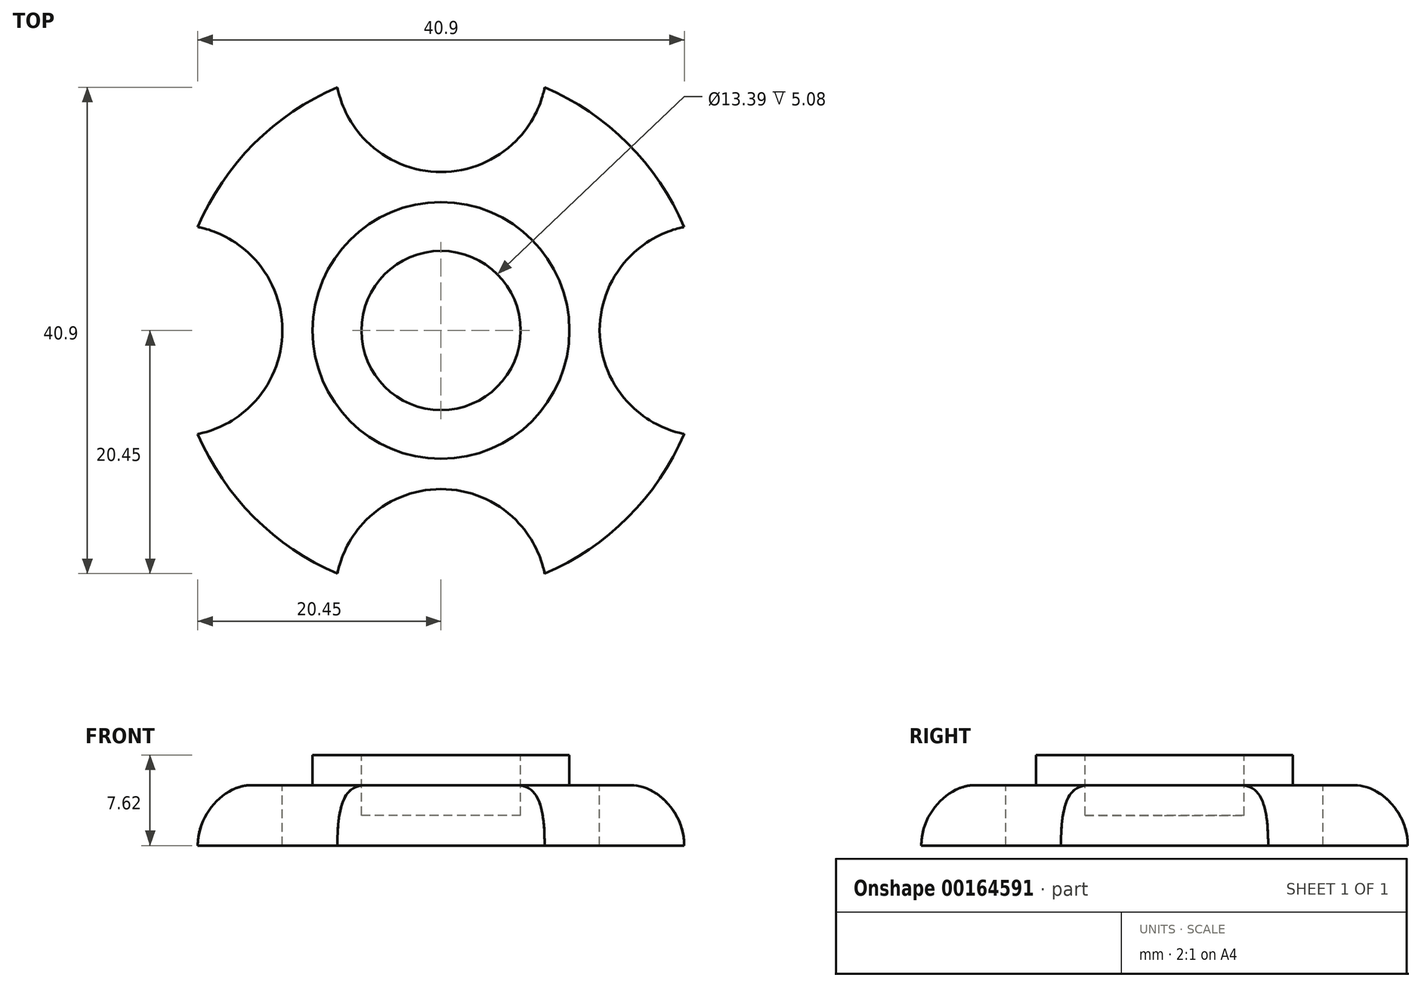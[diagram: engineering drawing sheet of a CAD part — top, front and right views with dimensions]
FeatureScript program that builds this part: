
annotation { "Feature Type Name" : "Feature", "Feature Type Description" : "" }
export const myFeature = defineFeature(function(context is Context, id is Id, definition is map)
    precondition{}
    {
        {
            var Q0;
            Q0=qCreatedBy(makeId("Top.planeOp"),FACE);
            var sketch = newSketch(context, id + "F0", { "sketchPlane" : qUnion([Q0])});
            skCircle(sketch, "E0", {"center": v(0, 0) * mm, "radius": 22.23 * mm});
            skSolve(sketch);
        }
        {
            var Q0;
            Q0 = qSketchRegion(id + "F0", true);
            extrude(context, id + "F1", {"entities" : qUnion([Q0]), "depth" : 5.08 * mm});
        }
        {
            var Q0;
            Q0=makeQuery(id+"F1.opExtrude","CAP_FACE",FACE,{"disambiguationData":[OSD([sQuery(id+"F0.wireOp",EDGE,"E0")])],"isStart":false});
            var sketch = newSketch(context, id + "F2", { "sketchPlane" : qUnion([Q0])});
            skCircle(sketch, "E1", {"center": v(0, 0) * mm, "radius": 10.8 * mm});
            skSolve(sketch);
        }
        {
            var Q0;
            Q0 = qSketchRegion(id + "F2", true);
            extrude(context, id + "F3", {"entities" : qUnion([Q0]), "operationType" : NewBodyOperationType.ADD, "depth" : 2.54 * mm});
        }
        {
            var Q0;
            Q0=makeQuery(id+"F3.opExtrude","CAP_FACE",FACE,{"disambiguationData":[OSD([sQuery(id+"F2.wireOp",EDGE,"E1")])],"isStart":false});
            var sketch = newSketch(context, id + "F4", { "sketchPlane" : qUnion([Q0])});
            skCircle(sketch, "E2", {"center": v(0, 0) * mm, "radius": 6.7 * mm});
            skSolve(sketch);
        }
        {
            var Q0;
            Q0 = qSketchRegion(id + "F4", true);
            extrude(context, id + "F5", {"entities" : qUnion([Q0]), "operationType" : NewBodyOperationType.REMOVE, "oppositeDirection" : true, "depth" : 5.08 * mm});
        }
        {
            var Q0;
            Q0=makeQuery(id+"F1.opExtrude","CAP_FACE",FACE,{"disambiguationData":[OSD([sQuery(id+"F0.wireOp",EDGE,"E0")])],"isStart":false});
            var sketch = newSketch(context, id + "F6", { "sketchPlane" : qUnion([Q0])});
            skCircle(sketch, "E3", {"center": v(0, 22.23) * mm, "radius": 8.9 * mm});
            skCircle(sketch, "E4", {"center": v(22.23, 0) * mm, "radius": 8.9 * mm});
            skCircle(sketch, "E5", {"center": v(0, -22.23) * mm, "radius": 8.9 * mm});
            skCircle(sketch, "E6", {"center": v(-22.23, 0) * mm, "radius": 8.9 * mm});
            skSolve(sketch);
        }
        {
            var Q0;
            Q0 = qSketchRegion(id + "F6", true);
            extrude(context, id + "F7", {"entities" : qUnion([Q0]), "operationType" : NewBodyOperationType.REMOVE, "oppositeDirection" : true, "depth" : 25.4 * mm});
        }
        {
            var Q0;
            {var subQ0=sQuery(id+"F0.wireOp",EDGE,"E0");Q0=makeQuery(id+"F7.boolean.opBoolean","SPLIT",EDGE,{"disambiguationData":[TD([makeQuery(id+"F1.opExtrude","SWEPT_FACE",FACE,{"disambiguationData":[OSD([subQ0])]}),makeQuery(id+"F1.opExtrude","CAP_FACE",FACE,{"disambiguationData":[OSD([subQ0])],"isStart":false}),makeQuery(id+"F7.opExtrude","SWEPT_FACE",FACE,{"disambiguationData":[OSD([sQuery(id+"F6.wireOp",EDGE,"E3")])]}),makeQuery(id+"F7.opExtrude","SWEPT_FACE",FACE,{"disambiguationData":[OSD([sQuery(id+"F6.wireOp",EDGE,"E6")])]})])],"derivedFrom":makeQuery(id+"F1.opExtrude","CAP_EDGE",EDGE,{"disambiguationData":[OSD([subQ0])],"isStart":false})});}
            var Q1;
            Q1=makeQuery(id+"F7.boolean.opBoolean","COPY",EDGE,{"derivedFrom":makeQuery(id+"F7.opExtrude","CAP_EDGE",EDGE,{"disambiguationData":[OSD([sQuery(id+"F6.wireOp",EDGE,"E3")])],"isStart":true})});
            var Q2;
            Q2=makeQuery(id+"F7.boolean.opBoolean","COPY",EDGE,{"derivedFrom":makeQuery(id+"F7.opExtrude","CAP_EDGE",EDGE,{"disambiguationData":[OSD([sQuery(id+"F6.wireOp",EDGE,"E4")])],"isStart":true})});
            var Q3;
            {var subQ0=sQuery(id+"F0.wireOp",EDGE,"E0");Q3=makeQuery(id+"F7.boolean.opBoolean","SPLIT",EDGE,{"disambiguationData":[TD([makeQuery(id+"F1.opExtrude","SWEPT_FACE",FACE,{"disambiguationData":[OSD([subQ0])]}),makeQuery(id+"F1.opExtrude","CAP_FACE",FACE,{"disambiguationData":[OSD([subQ0])],"isStart":false}),makeQuery(id+"F7.opExtrude","SWEPT_FACE",FACE,{"disambiguationData":[OSD([sQuery(id+"F6.wireOp",EDGE,"E3")])]}),makeQuery(id+"F7.opExtrude","SWEPT_FACE",FACE,{"disambiguationData":[OSD([sQuery(id+"F6.wireOp",EDGE,"E4")])]})])],"derivedFrom":makeQuery(id+"F1.opExtrude","CAP_EDGE",EDGE,{"disambiguationData":[OSD([subQ0])],"isStart":false})});}
            var Q4;
            Q4=makeQuery(id+"F7.boolean.opBoolean","COPY",EDGE,{"derivedFrom":makeQuery(id+"F7.opExtrude","CAP_EDGE",EDGE,{"disambiguationData":[OSD([sQuery(id+"F6.wireOp",EDGE,"E6")])],"isStart":true})});
            var Q5;
            {var subQ0=sQuery(id+"F0.wireOp",EDGE,"E0");Q5=makeQuery(id+"F7.boolean.opBoolean","SPLIT",EDGE,{"disambiguationData":[TD([makeQuery(id+"F1.opExtrude","SWEPT_FACE",FACE,{"disambiguationData":[OSD([subQ0])]}),makeQuery(id+"F1.opExtrude","CAP_FACE",FACE,{"disambiguationData":[OSD([subQ0])],"isStart":false}),makeQuery(id+"F7.opExtrude","SWEPT_FACE",FACE,{"disambiguationData":[OSD([sQuery(id+"F6.wireOp",EDGE,"E5")])]}),makeQuery(id+"F7.opExtrude","SWEPT_FACE",FACE,{"disambiguationData":[OSD([sQuery(id+"F6.wireOp",EDGE,"E6")])]})])],"derivedFrom":makeQuery(id+"F1.opExtrude","CAP_EDGE",EDGE,{"disambiguationData":[OSD([subQ0])],"isStart":false})});}
            var Q6;
            Q6=makeQuery(id+"F7.boolean.opBoolean","COPY",EDGE,{"derivedFrom":makeQuery(id+"F7.opExtrude","CAP_EDGE",EDGE,{"disambiguationData":[OSD([sQuery(id+"F6.wireOp",EDGE,"E5")])],"isStart":true})});
            var Q7;
            {var subQ0=sQuery(id+"F0.wireOp",EDGE,"E0");Q7=makeQuery(id+"F7.boolean.opBoolean","SPLIT",EDGE,{"disambiguationData":[TD([makeQuery(id+"F1.opExtrude","SWEPT_FACE",FACE,{"disambiguationData":[OSD([subQ0])]}),makeQuery(id+"F1.opExtrude","CAP_FACE",FACE,{"disambiguationData":[OSD([subQ0])],"isStart":false}),makeQuery(id+"F7.opExtrude","SWEPT_FACE",FACE,{"disambiguationData":[OSD([sQuery(id+"F6.wireOp",EDGE,"E4")])]}),makeQuery(id+"F7.opExtrude","SWEPT_FACE",FACE,{"disambiguationData":[OSD([sQuery(id+"F6.wireOp",EDGE,"E5")])]})])],"derivedFrom":makeQuery(id+"F1.opExtrude","CAP_EDGE",EDGE,{"disambiguationData":[OSD([subQ0])],"isStart":false})});}
            fillet(context, id + "F8", {"entities" : qUnion([Q0, Q1, Q2, Q3, Q4, Q5, Q6, Q7]), "radius" : 5.08 * mm, "tangentPropagation" : true, "allowEdgeOverflow" : false});
        }
    });
